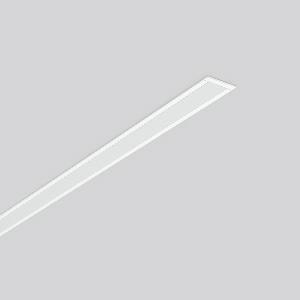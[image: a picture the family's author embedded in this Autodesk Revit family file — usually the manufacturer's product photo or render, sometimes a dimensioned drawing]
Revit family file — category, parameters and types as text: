
# Revit family: less_is_more_27_312178_002_76_eb57
name_source: partatom
category: Lighting Fixtures
units: mm (PartAtom-declared; Revit-internal decimal feet)

## family parameters
Cut with Voids When Loaded = No
Host = Face
Light Source = No
Part Type = Normal
Room Calculation Point = No
Round Connector Dimension = Use Diameter
Shared = No

## types (1)
- LESS IS MORE 27 (1 x LED Modul 830, 2900 lm, 3000)
    Apparent Load = 43 VA
    CIE Flux Codes = 48 79 96 100 100
    Color Rendering = 80
    Color Temperature = 3000
    Default Elevation = 1800 mm
    Description = Series: LESS IS MORE 27
Recessed ceiling and wall luminaire with slim design. Housing: extruded aluminium profile, powder-coated. End cap aluminium powder-coated. Diffuser made of non-yellowing plastic (PMMA), opal. Suitable for Recessed ceiling mounting, wall (recessed). External driver with connecting cable. 
Colour: traffic white, matt (RAL 9016)
Length: 1514 mm
Width: 38 mm
Height: 2 mm
Cut-out length: 1506 mm
Cut-out width: 30 mm
Recess height: 45-60 mm
Luminaire: recess height: 37 mm
Lamp: LED
Socket: without socket
Colour temperature: 3000K
Colour rendering index (CRI): 82
System power: 43 W
Rated luminous flux: 2900 lm
Luminous efficiency: 67 lm/W
Control gear: Voltage converter, DALI dim.
Protection class: II
Type of protection: IP 20
    Height = 0 mm  [stored 0 ft]
    Lamp = 1 x LED Modul 830
    Lamp Light Flux = 2900 lm
    Lamp count = 1
    Length = 1514 mm
    Lifetime = 50000 h
    Luminous efficacy = 67 lm/W
    Manufacturer = RZB
    ModVariant = No
    Model = 312178.002.76
    Mounting Place = Ceiling, Wall
    Mounting Type = Recessed
    Number of Poles = 1
    OnlyDefault = Yes
    Power Factor = 1
    Product Name = LESS IS MORE 27
    Product group = Recessed LED linear luminaires
    ProductGroupID = 407
    Protection Class = Protection class II
    Protection Degree = IP 20
    RLX_Detail_Level = 1
    RLX_Emergency_Light_Flux = 0 lm
    RLX_Emergency_Type = 0
    RLX_Emergency_Type_DB = No
    RlxData = <blob elided: 21625 chars, md5=d1ea2bc4>
    Socket = socket
    Standby Power = 0 W
    System Light Flux = 2900 lm
    System Power = 43 W
    Type Comments = Product without accessories
    Type Image = 312176.002.jpg
    URL = http://relux.com
    VarID = ---
    Voltage = 230 V
    Voltage Range = 220-240 V
    Weight = 0.00 kg
    Width = 38 mm

note: [stored X ft] marks values corroborated as IEEE doubles in the binary element streams (Revit-internal decimal feet)

## geometry (parser evidence)
native form markers: Blend x4, Sweep x11
no freeform markers — native parametric forms only
